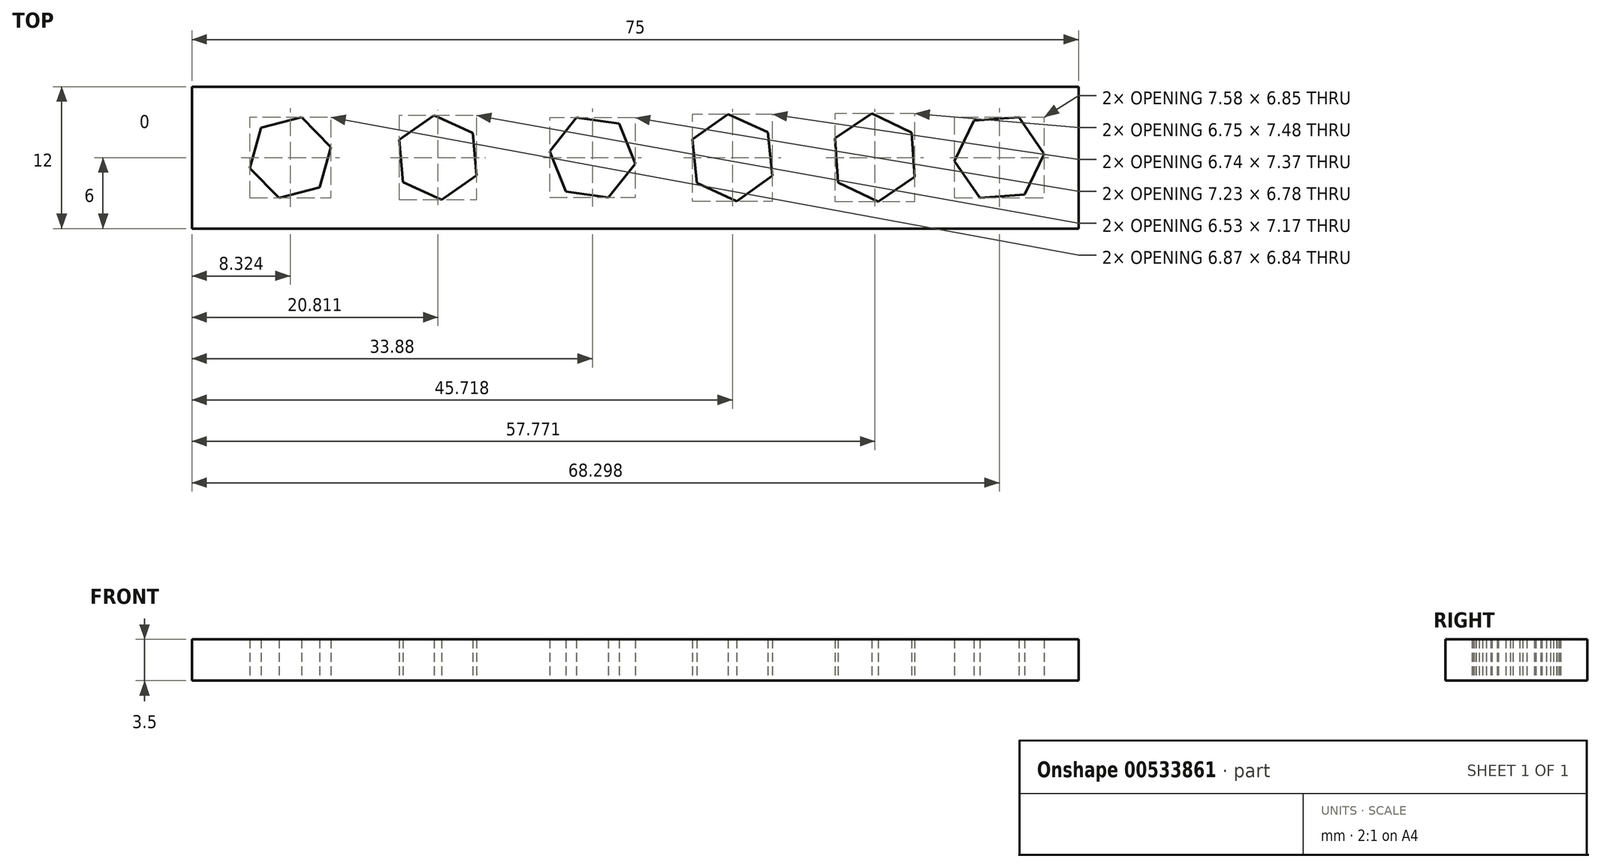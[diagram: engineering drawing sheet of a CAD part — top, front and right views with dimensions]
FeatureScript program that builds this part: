
annotation { "Feature Type Name" : "Feature", "Feature Type Description" : "" }
export const myFeature = defineFeature(function(context is Context, id is Id, definition is map)
    precondition{}
    {
        {
            var Q0;
            Q0=qCreatedBy(makeId("Top.planeOp"),FACE);
            var sketch = newSketch(context, id + "F0", { "sketchPlane" : qUnion([Q0])});
            skLineSegment(sketch, "E0.bottom", {"start": v(37.5, 6) * mm, "end": v(-37.5, 6) * mm});
            skLineSegment(sketch, "E0.top", {"start": v(37.5, -6) * mm, "end": v(-37.5, -6) * mm});
            skLineSegment(sketch, "E0.left", {"start": v(37.5, 6) * mm, "end": v(37.5, -6) * mm});
            skLineSegment(sketch, "E0.right", {"start": v(-37.5, 6) * mm, "end": v(-37.5, -6) * mm});
            skPoint(sketch, "E0.middle", {"position": v(0, 0) * mm});
            skCircle(sketch, "E1.cCircle", {"center": v(-29.18, 0) * mm, "radius": 3.55 * mm, "construction": true});
            skLineSegment(sketch, "E1.0", {"start": v(-28.23, 3.42) * mm, "end": v(-25.74, 0.89) * mm});
            skLineSegment(sketch, "E1.1", {"start": v(-25.74, 0.89) * mm, "end": v(-26.69, -2.53) * mm});
            skLineSegment(sketch, "E1.2", {"start": v(-26.69, -2.53) * mm, "end": v(-30.13, -3.42) * mm});
            skLineSegment(sketch, "E1.3", {"start": v(-30.13, -3.42) * mm, "end": v(-32.61, -0.89) * mm});
            skLineSegment(sketch, "E1.4", {"start": v(-32.61, -0.89) * mm, "end": v(-31.66, 2.53) * mm});
            skLineSegment(sketch, "E1.5", {"start": v(-31.66, 2.53) * mm, "end": v(-28.23, 3.42) * mm});
            skCircle(sketch, "E2.cCircle", {"center": v(-16.69, 0) * mm, "radius": 3.6 * mm, "construction": true});
            skLineSegment(sketch, "E2.0", {"start": v(-17, 3.59) * mm, "end": v(-13.74, 2.07) * mm});
            skLineSegment(sketch, "E2.1", {"start": v(-13.74, 2.07) * mm, "end": v(-13.42, -1.52) * mm});
            skLineSegment(sketch, "E2.2", {"start": v(-13.42, -1.52) * mm, "end": v(-16.37, -3.59) * mm});
            skLineSegment(sketch, "E2.3", {"start": v(-16.37, -3.59) * mm, "end": v(-19.63, -2.07) * mm});
            skLineSegment(sketch, "E2.4", {"start": v(-19.63, -2.07) * mm, "end": v(-19.95, 1.52) * mm});
            skLineSegment(sketch, "E2.5", {"start": v(-19.95, 1.52) * mm, "end": v(-17, 3.59) * mm});
            skCircle(sketch, "E3.cCircle", {"center": v(-3.62, 0) * mm, "radius": 3.65 * mm, "construction": true});
            skLineSegment(sketch, "E3.0", {"start": v(-4.98, 3.39) * mm, "end": v(-1.36, 2.87) * mm});
            skLineSegment(sketch, "E3.1", {"start": v(-1.36, 2.87) * mm, "end": v(0, -0.52) * mm});
            skLineSegment(sketch, "E3.2", {"start": v(0, -0.52) * mm, "end": v(-2.26, -3.39) * mm});
            skLineSegment(sketch, "E3.3", {"start": v(-2.26, -3.39) * mm, "end": v(-5.88, -2.87) * mm});
            skLineSegment(sketch, "E3.4", {"start": v(-5.88, -2.87) * mm, "end": v(-7.23, 0.52) * mm});
            skLineSegment(sketch, "E3.5", {"start": v(-7.23, 0.52) * mm, "end": v(-4.98, 3.39) * mm});
            skCircle(sketch, "E4.cCircle", {"center": v(8.22, 0) * mm, "radius": 3.7 * mm, "construction": true});
            skLineSegment(sketch, "E4.0", {"start": v(7.86, 3.68) * mm, "end": v(11.23, 2.15) * mm});
            skLineSegment(sketch, "E4.1", {"start": v(11.23, 2.15) * mm, "end": v(11.59, -1.53) * mm});
            skLineSegment(sketch, "E4.2", {"start": v(11.59, -1.53) * mm, "end": v(8.58, -3.68) * mm});
            skLineSegment(sketch, "E4.3", {"start": v(8.58, -3.68) * mm, "end": v(5.2, -2.15) * mm});
            skLineSegment(sketch, "E4.4", {"start": v(5.2, -2.15) * mm, "end": v(4.85, 1.53) * mm});
            skLineSegment(sketch, "E4.5", {"start": v(4.85, 1.53) * mm, "end": v(7.86, 3.68) * mm});
            skCircle(sketch, "E5.cCircle", {"center": v(20.27, 0) * mm, "radius": 3.75 * mm, "construction": true});
            skLineSegment(sketch, "E5.0", {"start": v(20, 3.74) * mm, "end": v(23.38, 2.1) * mm});
            skLineSegment(sketch, "E5.1", {"start": v(23.38, 2.1) * mm, "end": v(23.64, -1.64) * mm});
            skLineSegment(sketch, "E5.2", {"start": v(23.64, -1.64) * mm, "end": v(20.54, -3.74) * mm});
            skLineSegment(sketch, "E5.3", {"start": v(20.54, -3.74) * mm, "end": v(17.17, -2.1) * mm});
            skLineSegment(sketch, "E5.4", {"start": v(17.17, -2.1) * mm, "end": v(16.9, 1.64) * mm});
            skLineSegment(sketch, "E5.5", {"start": v(16.9, 1.64) * mm, "end": v(20, 3.74) * mm});
            skCircle(sketch, "E6.cCircle", {"center": v(30.8, 0) * mm, "radius": 3.8 * mm, "construction": true});
            skPoint(sketch, "E6.cCircle.centerSnap0", {"position": v(37.5, 0) * mm});
            skLineSegment(sketch, "E6.0", {"start": v(32.44, 3.43) * mm, "end": v(34.59, 0.3) * mm});
            skLineSegment(sketch, "E6.1", {"start": v(34.59, 0.3) * mm, "end": v(32.95, -3.14) * mm});
            skLineSegment(sketch, "E6.2", {"start": v(32.95, -3.14) * mm, "end": v(29.16, -3.43) * mm});
            skLineSegment(sketch, "E6.3", {"start": v(29.16, -3.43) * mm, "end": v(27, -0.3) * mm});
            skLineSegment(sketch, "E6.4", {"start": v(27, -0.3) * mm, "end": v(28.65, 3.14) * mm});
            skLineSegment(sketch, "E6.5", {"start": v(28.65, 3.14) * mm, "end": v(32.44, 3.43) * mm});
            skSolve(sketch);
        }
        {
            var Q0;
            Q0=makeQuery(id+"F0.imprint","IMPRINT",FACE,{"disambiguationData":[TD([[makeQuery(id+"F0.imprint","IMPRINT",EDGE,{"derivedFrom":sQuery(id+"F0.wireOp",EDGE,"E0.bottom")}),1.0]])]});
            extrude(context, id + "F1", {"entities" : qUnion([Q0]), "depth" : 3.5 * mm, "offsetDistance" : 25 * mm});
        }
    });
